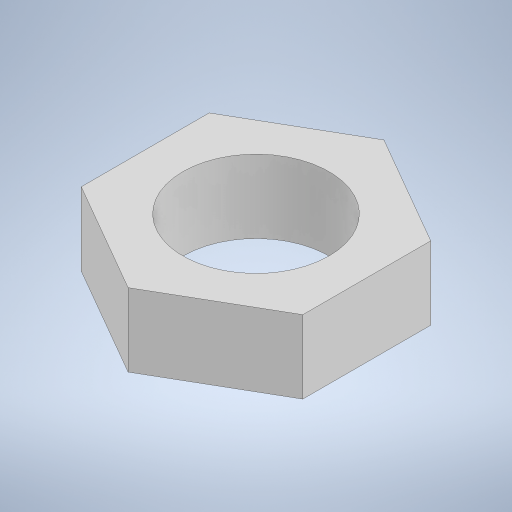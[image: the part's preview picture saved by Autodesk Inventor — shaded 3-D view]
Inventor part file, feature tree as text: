
AUTODESK INVENTOR PART (.ipt)
format: ipt  version: 2024.2 (Build 282272000, 272)  size: 211,968 bytes
history: native  units: mm
features: extrude x1, sketch x1
ambient origin geometry x8: Origin, YZ Plane, XZ Plane, XY Plane, X Axis, Y Axis, Z Axis, Center Point
bodies: Solid1 (feature_tree)
feature tree (2):
  extrude  "Extrusion1"  Depth=1.0mm
  sketch  "Sketch1"  dims[d0=2.0mm d1=3.5mm d2=1.0mm d3=0.0mm]
